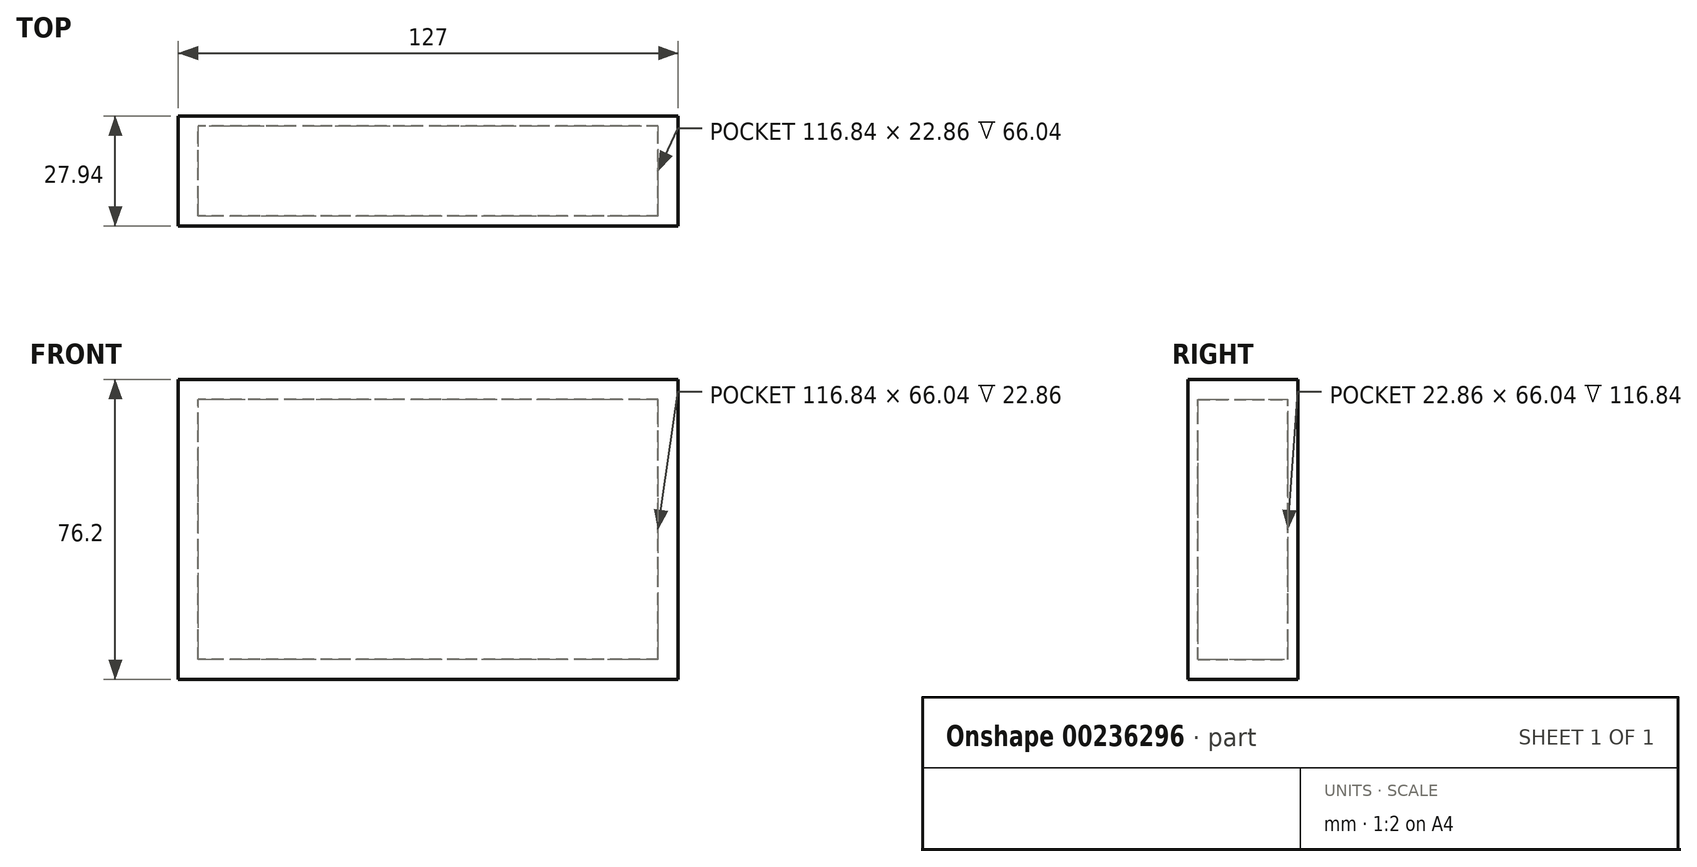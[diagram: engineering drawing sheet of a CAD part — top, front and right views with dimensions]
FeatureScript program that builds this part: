
annotation { "Feature Type Name" : "Feature", "Feature Type Description" : "" }
export const myFeature = defineFeature(function(context is Context, id is Id, definition is map)
    precondition{}
    {
        {
            var Q0;
            Q0=qCreatedBy(makeId("Front.planeOp"),FACE);
            var sketch = newSketch(context, id + "F4", { "sketchPlane" : qUnion([Q0])});
            skLineSegment(sketch, "E0.bottom", {"start": v(63.5, -38.1) * mm, "end": v(-63.5, -38.1) * mm});
            skLineSegment(sketch, "E0.top", {"start": v(63.5, 38.1) * mm, "end": v(-63.5, 38.1) * mm});
            skLineSegment(sketch, "E0.left", {"start": v(63.5, -38.1) * mm, "end": v(63.5, 38.1) * mm});
            skLineSegment(sketch, "E0.right", {"start": v(-63.5, -38.1) * mm, "end": v(-63.5, 38.1) * mm});
            skPoint(sketch, "E0.middle", {"position": v(0, 0) * mm});
            skSolve(sketch);
        }
        {
            var Q0;
            Q0 = qSketchRegion(id + "F4", true);
            extrude(context, id + "F5", {"entities" : qUnion([Q0]), "depth" : 25.4 * mm});
        }
        {
            var Q0;
            Q0=makeQuery(id+"F5.opExtrude","CAP_FACE",FACE,{"disambiguationData":[OSD([sQuery(id+"F4.wireOp",EDGE,"E0.bottom"),sQuery(id+"F4.wireOp",EDGE,"E0.top"),sQuery(id+"F4.wireOp",EDGE,"E0.left"),sQuery(id+"F4.wireOp",EDGE,"E0.right")])],"isStart":false});
            shell(context, id + "F6", {"entities" : qUnion([Q0]), "thickness" : 2.54 * mm});
        }
        {
            var Q0;
            Q0=makeQuery(id+"F6.opShell","OFFSET_FACE",FACE,{"disambiguationData":[OSD([sQuery(id+"F4.wireOp",EDGE,"E0.bottom"),sQuery(id+"F4.wireOp",EDGE,"E0.top"),sQuery(id+"F4.wireOp",EDGE,"E0.left"),sQuery(id+"F4.wireOp",EDGE,"E0.right")])]});
            var sketch = newSketch(context, id + "F0", { "sketchPlane" : qUnion([Q0])});
            skLineSegment(sketch, "E1.0", {"start": v(60.96, 35.56) * mm, "end": v(-60.96, 35.56) * mm});
            skLineSegment(sketch, "E2.0", {"start": v(-60.96, -35.56) * mm, "end": v(-60.96, 35.56) * mm});
            skLineSegment(sketch, "E3.0", {"start": v(60.96, -35.56) * mm, "end": v(-60.96, -35.56) * mm});
            skLineSegment(sketch, "E4.0", {"start": v(60.96, -35.56) * mm, "end": v(60.96, 35.56) * mm});
            skLineSegment(sketch, "E5.0", {"start": v(58.42, 33.02) * mm, "end": v(-58.42, 33.02) * mm});
            skLineSegment(sketch, "E5.1", {"start": v(58.42, -33.02) * mm, "end": v(58.42, 33.02) * mm});
            skLineSegment(sketch, "E5.2", {"start": v(58.42, -33.02) * mm, "end": v(-58.42, -33.02) * mm});
            skLineSegment(sketch, "E5.3", {"start": v(-58.42, -33.02) * mm, "end": v(-58.42, 33.02) * mm});
            skSolve(sketch);
        }
        {
            var Q0;
            Q0=makeQuery(id+"F0.imprint","IMPRINT",FACE,{"disambiguationData":[TD([[makeQuery(id+"F0.imprint","IMPRINT",EDGE,{"derivedFrom":sQuery(id+"F0.wireOp",EDGE,"E1.0")}),1.0]])]});
            extrude(context, id + "F1", {"entities" : qUnion([Q0]), "operationType" : NewBodyOperationType.ADD, "depth" : 12.7 * mm});
        }
        {
            var Q0;
            Q0=makeQuery(id+"F1.opExtrude","CAP_FACE",FACE,{"disambiguationData":[OSD([sQuery(id+"F0.wireOp",EDGE,"E1.0"),sQuery(id+"F0.wireOp",EDGE,"E2.0"),sQuery(id+"F0.wireOp",EDGE,"E3.0"),sQuery(id+"F0.wireOp",EDGE,"E4.0"),sQuery(id+"F0.wireOp",EDGE,"E5.0"),sQuery(id+"F0.wireOp",EDGE,"E5.1"),sQuery(id+"F0.wireOp",EDGE,"E5.2"),sQuery(id+"F0.wireOp",EDGE,"E5.3")])],"isStart":false});
            extrude(context, id + "F2", {"entities" : qUnion([Q0]), "depth" : 10.16 * mm});
        }
        {
            var Q0;
            Q0=makeQuery(id+"F5.opExtrude","CAP_FACE",FACE,{"disambiguationData":[OSD([sQuery(id+"F4.wireOp",EDGE,"E0.bottom"),sQuery(id+"F4.wireOp",EDGE,"E0.top"),sQuery(id+"F4.wireOp",EDGE,"E0.left"),sQuery(id+"F4.wireOp",EDGE,"E0.right")])],"isStart":false});
            var sketch = newSketch(context, id + "F3", { "sketchPlane" : qUnion([Q0])});
            skLineSegment(sketch, "E6.0", {"start": v(63.5, -38.1) * mm, "end": v(63.5, 38.1) * mm});
            skLineSegment(sketch, "E7.0", {"start": v(63.5, 38.1) * mm, "end": v(-63.5, 38.1) * mm});
            skLineSegment(sketch, "E8.0", {"start": v(-63.5, -38.1) * mm, "end": v(-63.5, 38.1) * mm});
            skLineSegment(sketch, "E9.0", {"start": v(63.5, -38.1) * mm, "end": v(-63.5, -38.1) * mm});
            skSolve(sketch);
        }
        {
            var Q0;
            Q0 = qSketchRegion(id + "F3", true);
            extrude(context, id + "F7", {"entities" : qUnion([Q0]), "operationType" : NewBodyOperationType.ADD, "depth" : 2.54 * mm});
        }
    });
